# Revit family: Lighting_Fixture-Focal_Point-Nivo_Acoustic_Unlit new
name_source: partatom
category: Lighting Fixtures
revit_build: Autodesk Revit 2017 (Build: 20160225_1515(x64)
units: mm (PartAtom-declared; Revit-internal decimal feet)

## family parameters
Cut with Voids When Loaded = Yes
Host = Face
Light Source = No
OmniClass Number = 23.80.70.11.11
OmniClass Title = General Luminaries, Non Directional
Part Type = Normal
Room Calculation Point = No
Round Connector Dimension = Use Diameter
Shared = No

## types (16) — shared parameters
Acoustic Element Material = Polyester-Focal_Point-Standard_Color-SLT-Slate
Apparent Load = 0 VA
Assembly Code = C2050.80
Default Elevation = 0' - 0"
Description = Sound absorbing Nivo tiles drop 7" down from the ceiling in 1" increments.
Installation and Service URL = Contact Focal Point for more information
Keynote = 09 84 00
Lamp = Unlit
Length = 2' - 0"
Manufacturer = Focal Point L.L.C.
Manufacturer Fax Number = (773) 247-8484
Material = Architect to Select
Product Documentation Link = Contact Focal Point for more information
Product Name = Nivo Acoustic
Product Page URL = Contact Focal Point for more information
URL = https://www.focalpointlights.com
Version = 2017 v1.0a
Warranty URL = Contact Focal Point for more information
Wattage Comments = 0
Width = 2' - 0"

## per-type parameters (varying)
| type | Constraints | Drop | Model | Mounting | Profile |
| Nivo Acoustic Tile - Flush - 15/16" Layin | 0 | 0' - 0" | AUNV-22-Z-G1-CP-XXX | 15/16" Layin | Flush |
| Nivo Acoustic Tile - 7" Drop - 9/16" Layin | 7 | 0' - 7" | AUNV-22-7D-G2-CP-XXX | 9/16" Layin | 7" Drop |
| Nivo Acoustic Tile - 7" Drop - 15/16" Layin | 7 | 0' - 7" | AUNV-22-7D-G1-CP-XXX | 15/16" Layin | 7" Drop |
| Nivo Acoustic Tile - 6" Drop - 9/16" Layin | 6 | 0' - 6" | AUNV-22-6D-G2-CP-XXX | 9/16" Layin | 6" Drop |
| Nivo Acoustic Tile - 6" Drop - 15/16" Layin | 6 | 0' - 6" | AUNV-22-6D-G1-CP-XXX | 15/16" Layin | 6" Drop |
| Nivo Acoustic Tile - 5" Drop - 9/16" Layin | 5 | 0' - 5" | AUNV-22-5D-G2-CP-XXX | 9/16" Layin | 5" Drop |
| Nivo Acoustic Tile - 5" Drop - 15/16" Layin | 5 | 0' - 5" | AUNV-22-5D-G1-CP-XXX | 15/16" Layin | 5" Drop |
| Nivo Acoustic Tile - 4" Drop - 9/16" Layin | 4 | 0' - 4" | AUNV-22-4D-G2-CP-XXX | 9/16" Layin | 4" Drop |
| Nivo Acoustic Tile - 4" Drop - 15/16" Layin | 4 | 0' - 4" | AUNV-22-4D-G1-CP-XXX | 15/16" Layin | 4" Drop |
| Nivo Acoustic Tile - 3" Drop - 9/16" Layin | 3 | 0' - 3" | AUNV-22-3D-G2-CP-XXX | 9/16" Layin | 3" Drop |
| Nivo Acoustic Tile - 3" Drop - 15/16" Layin | 3 | 0' - 3" | AUNV-22-3D-G1-CP-XXX | 15/16" Layin | 3" Drop |
| Nivo Acoustic Tile - 2" Drop - 9/16" Layin | 2 | 0' - 2" | AUNV-22-2D-G2-CP-XXX | 9/16" Layin | 2" Drop |
| Nivo Acoustic Tile - 2" Drop - 15/16" Layin | 2 | 0' - 2" | AUNV-22-2D-G1-CP-XXX | 15/16" Layin | 2" Drop |
| Nivo Acoustic Tile - 1" Drop - 9/16" Layin | 1 | 0' - 1" | AUNV-22-1D-G2-CP-XXX | 9/16" Layin | 1" Drop |
| Nivo Acoustic Tile - 1" Drop - 15/16" Layin | 1 | 0' - 1" | AUNV-22-1D-G1-CP-XXX | 15/16" Layin | 1" Drop |
| Nivo Acoustic Tile - Flush - 9/16" Layin | 0 | 0' - 0" | AUNV-22-Z-G2-CP-XXX | 9/16" Layin | Flush |

## geometry (parser evidence)
native form markers: Sweep x1
no freeform markers — native parametric forms only
